# Revit family: 41-60-003-DN200
name_source: partatom
category: Pipe Accessories
units: mm (PartAtom-declared; Revit-internal decimal feet)

## family parameters
Always vertical = Yes
Cut with Voids When Loaded = No
Part Type = Valve - Breaks Into
Round Connector Dimension = Use Diameter
Shared = No
Work Plane-Based = No

## types (1)
- DN200
    DN = 200 mm  [stored 0.656168 ft]
    DN 200_PN10 = 41-200-60-008
    DN150 = Yes
    DN200_PN16 = 41-200-60-018
    Description_ = AVK_SWING_CHECK_VALVE
    FOD = 170 mm  [stored 0.557743 ft]
    H3 = 412 mm  [stored 1.35171 ft]
    ID = 100 mm  [stored 0.328084 ft]
    L = 500 mm  [stored 1.64042 ft]
    RF = 132 mm  [stored 0.433071 ft]
    URL product pages = https://www.avkvalves.com
    W = 338 mm  [stored 1.10892 ft]

note: [stored X ft] marks values corroborated as IEEE doubles in the binary element streams (Revit-internal decimal feet)

## geometry (parser evidence)
native form markers: Sweep x4
no freeform markers — native parametric forms only
